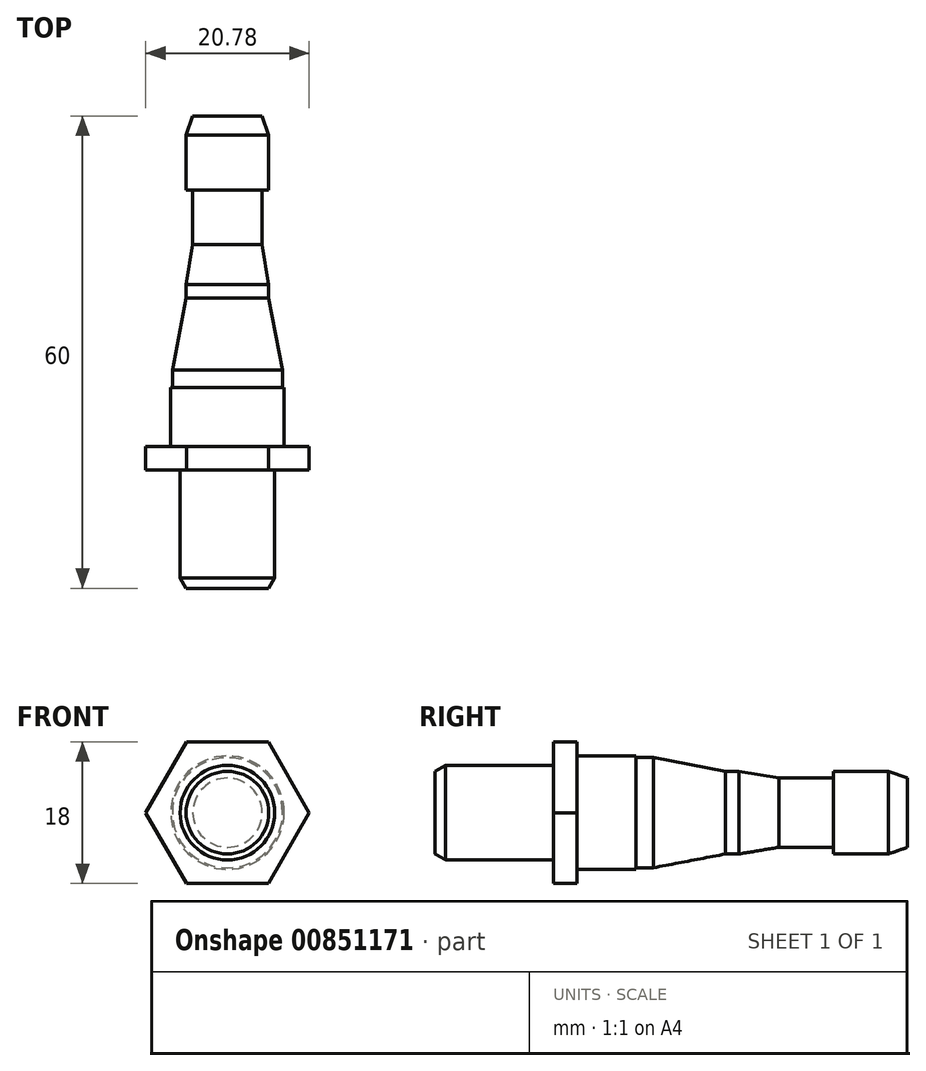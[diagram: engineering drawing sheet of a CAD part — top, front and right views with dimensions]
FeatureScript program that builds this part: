
annotation { "Feature Type Name" : "Feature", "Feature Type Description" : "" }
export const myFeature = defineFeature(function(context is Context, id is Id, definition is map)
    precondition{}
    {
        {
            var Q0;
            Q0=qCreatedBy(makeId("Right.planeOp"),FACE);
            var sketch = newSketch(context, id + "F0", { "sketchPlane" : qUnion([Q0])});
            skLineSegment(sketch, "E0", {"start": v(0, 0) * mm, "end": v(0, 6) * mm});
            skLineSegment(sketch, "E1", {"start": v(0, 6) * mm, "end": v(15, 6) * mm});
            skLineSegment(sketch, "E2", {"start": v(15, 6) * mm, "end": v(15, 7.2) * mm});
            skLineSegment(sketch, "E3", {"start": v(60, 4.4) * mm, "end": v(60, 0) * mm});
            skLineSegment(sketch, "E4", {"start": v(60, 0) * mm, "end": v(0, 0) * mm});
            skLineSegment(sketch, "E5", {"start": v(60, 4.4) * mm, "end": v(57.57, 5.25) * mm});
            skLineSegment(sketch, "E6", {"start": v(57.57, 5.25) * mm, "end": v(50.57, 5.25) * mm});
            skLineSegment(sketch, "E7", {"start": v(50.57, 5.25) * mm, "end": v(50.57, 4.4) * mm});
            skLineSegment(sketch, "E8", {"start": v(50.57, 4.4) * mm, "end": v(43.66, 4.4) * mm});
            skLineSegment(sketch, "E9", {"start": v(43.66, 4.4) * mm, "end": v(38.57, 5.25) * mm});
            skLineSegment(sketch, "E10", {"start": v(38.57, 5.25) * mm, "end": v(36.88, 5.25) * mm});
            skLineSegment(sketch, "E11", {"start": v(36.88, 5.25) * mm, "end": v(36.88, 5.25) * mm});
            skLineSegment(sketch, "E12", {"start": v(36.88, 5.25) * mm, "end": v(27.7, 7) * mm});
            skLineSegment(sketch, "E13", {"start": v(27.7, 7) * mm, "end": v(25.5, 7) * mm});
            skLineSegment(sketch, "E14", {"start": v(25.5, 7) * mm, "end": v(25.5, 7.2) * mm});
            skLineSegment(sketch, "E15", {"start": v(25.5, 7.2) * mm, "end": v(15, 7.2) * mm});
            skSolve(sketch);
        }
        {
            var Q0;
            Q0=qCreatedBy(makeId("Right.planeOp"),FACE);
            var sketch = newSketch(context, id + "F1", { "sketchPlane" : qUnion([Q0])});
            skLineSegment(sketch, "E16", {"start": v(-75.24, 0) * mm, "end": v(74.74, 0) * mm, "construction": true});
            skSolve(sketch);
        }
        {
            var Q0;
            Q0=makeQuery(id+"F0.imprint","IMPRINT",FACE,{"disambiguationData":[TD([[makeQuery(id+"F0.imprint","IMPRINT",EDGE,{"derivedFrom":sQuery(id+"F0.wireOp",EDGE,"E0")}),-1.0]])]});
            var Q1;
            Q1=sQuery(id+"F1.wireOp",EDGE,"E16");
            revolve(context, id + "F2", {"surfaceOperationType" : NewSurfaceOperationType.NEW, "entities" : qUnion([Q0]), "axis" : qUnion([Q1]), "revolveType" : RevolveType.FULL});
        }
        {
            var Q0;
            Q0=makeQuery(id+"F2.opRevolve","SWEPT_FACE",FACE,{"disambiguationData":[OSD([sQuery(id+"F0.wireOp",EDGE,"E2")])]});
            var sketch = newSketch(context, id + "F3", { "sketchPlane" : qUnion([Q0])});
            skCircle(sketch, "E17.cCircle", {"center": v(0, 0) * mm, "radius": 9 * mm, "construction": true});
            skLineSegment(sketch, "E17.0", {"start": v(-5.2, 9) * mm, "end": v(5.2, 9) * mm});
            skLineSegment(sketch, "E17.1", {"start": v(5.2, 9) * mm, "end": v(10.4, 0) * mm});
            skLineSegment(sketch, "E17.2", {"start": v(10.4, 0) * mm, "end": v(5.2, -9) * mm});
            skLineSegment(sketch, "E17.3", {"start": v(5.2, -9) * mm, "end": v(-5.2, -9) * mm});
            skLineSegment(sketch, "E17.4", {"start": v(-5.2, -9) * mm, "end": v(-10.4, 0) * mm});
            skLineSegment(sketch, "E17.5", {"start": v(-10.4, 0) * mm, "end": v(-5.2, 9) * mm});
            skPoint(sketch, "E17.0.midPoint", {"position": v(0, 9) * mm});
            skSolve(sketch);
        }
        {
            var Q0;
            Q0=makeQuery(id+"F3.imprint","IMPRINT",FACE,{"disambiguationData":[TD([[makeQuery(id+"F3.imprint","IMPRINT",EDGE,{"derivedFrom":sQuery(id+"F3.wireOp",EDGE,"E17.0")}),-1.0]])]});
            extrude(context, id + "F4", {"entities" : qUnion([Q0]), "operationType" : NewBodyOperationType.ADD, "oppositeDirection" : true, "depth" : 3 * mm, "offsetDistance" : 25 * mm});
        }
        {
            var Q0;
            Q0=makeQuery(id+"F2.opRevolve","SWEPT_EDGE",EDGE,{"disambiguationData":[OSD([sQuery(id+"F0.wireOp",EDGE,"E0"),sQuery(id+"F0.wireOp",EDGE,"E1")])]});
            chamfer(context, id + "F5", {"entities" : qUnion([Q0]), "chamferType" : ChamferType.OFFSET_ANGLE, "width" : .75 * mm, "oppositeDirection" : false, "angle" : 60 * degree, "tangentPropagation" : true});
        }
    });
